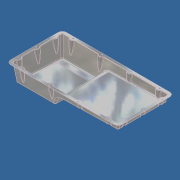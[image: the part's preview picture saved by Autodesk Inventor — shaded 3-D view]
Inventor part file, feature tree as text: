
AUTODESK INVENTOR PART (.ipt)
format: ipt  version: unknown  size: 1,103,872 bytes
history: native  units: mm (DEFAULTED — no unit token found)
features: sketch x8, fillet x6, extrude x5, shell x2, mirror x2, hole x2, split x1
ambient origin geometry x8: Origin, YZ Plane, XZ Plane, XY Plane, X Axis, Y Axis, Z Axis, Center Point
feature tree (26):
  extrude  "Extrusion1"  Depth=254.0mm
  extrude  "Extrusion2"  Depth=203.2mm
  split  "Split1"
  fillet  "Fillet4"  Radius=50.8mm
  fillet  "Fillet1"  Radius=3.490659mm
  fillet  "Fillet2"  Radius=19.05mm
  shell  "Shell1"  Thickness=12.7mm
  extrude  "Extrusion6"  Depth=50.8mm
  mirror  "Mirror1"
  extrude  "Extrusion7"  Depth=2.54mm TaperAngle=0.0deg
  mirror  "Mirror2"
  shell  "Shell5"  Thickness=1.22173mm
  fillet  "Fillet10"  Radius=12.7mm
  hole  "Hole3"  [1 undecoded]
  fillet  "Fillet15"  Radius=1.905mm
  extrude  "Extrusion9"  Depth=12.7mm
  fillet  "Fillet13"  Radius=38.1mm
  hole  "Hole2"  [1 undecoded]
  sketch  "Sketch2"  dims[d0=508.0mm d1=254.0mm]
  sketch  "Sketch3"  dims[d2=50.8mm d3=0.0mm d4=203.2mm d5=50.8mm d6=0.0mm d7=3.490659mm d9=19.05mm d10=19.05mm d11=12.7mm d15=0.261799mm]
  sketch  "Sketch4"  dims[d16=0.523599mm d17=50.8mm]
  sketch  "Sketch8"  dims[d18=127.0mm d35=2.54mm d36=0.0mm d42=1.22173mm d44=12.7mm]
  sketch  "Sketch9"  dims[d47=2.54mm d48=0.0mm d52=3.81mm d64=1.905mm]
  sketch  "Sketch12"  dims[d65=10.414mm d66=9.525mm d67=6.35mm d68=60.0deg d69=19.05mm d70=20.594885mm d73=12.7mm d76=38.1mm]
  sketch  "Sketch13"  dims[d77=7.62mm d79=25.4mm]
  sketch  "Sketch14"  dims[d80=12.7mm d81=10.0mm d83=25.4mm d84=40.0mm d86=131.137959mm d88=7.62mm d89=25.4mm d90=25.4mm d91=1.27mm d93=6.35mm d94=12.7mm d95=9.525mm d96=6.35mm d97=14.3117mm d98=19.05mm d99=20.594885mm d100=0.508mm d101=1.797004mm d102=5.099004mm d104=25.4mm d105=3.81mm d106=0.0mm d107=12.7mm]
note: 2 required parameter values undecoded (feature->parameter linkage not recoverable at this tier; creation-order binding heuristic only, values carry confidence <= 0.55)
